# Revit family: 28798_2
name_source: partatom
category: Generic Models
units: mm (PartAtom-declared; Revit-internal decimal feet)

## family parameters
Always vertical = Yes
Can host rebar = No
Cut with Voids When Loaded = No
Part Type = Normal
Room Calculation Point = No
Round Connector Dimension = Use Diameter
Shared = Yes
Work Plane-Based = No

## types (1)
- 28798
    4.010.00.2 Sheet number of the guideline = 4
    4.010.00.4 Manufacturer name = KESSEL AG
    4.010.00.8 Producer ID number = 4026092000007
    4.100.00.4 Product indentification = Entwässerung
    4.100.00.6 Product classification = Hebeanlagen
    4.110.00.4 Product indentification = Hebeanlage Aqualift F Basic
    4.110.00.5 Main groups of wares = Aqualift F Basic
    4.110.00.6 Product classification = Hebeanlage
    4.500.00.3 Variant / Variant type / Accessories-name = Kunststoff
    4.700.00.10 Phase = 1/N/PE 230V
    4.700.00.11 Stern-/Dreieck-Anlaufschaltung bei Dreiphasenanschluss oder Drehstrom = nein
    4.700.00.12 Frequency = 50
    4.700.00.13 Type of protection = IP 68
    4.700.00.14 Heat class = F
    4.700.00.16 Maximum temperature of pumped medium = 40 °C
    4.700.00.17 Minimum temperature of pumped medium = 0 °C
    4.700.00.23 Nominal speed of motor = 10.76391
    4.700.00.24 Nominal speed / maximum speed n = 43.333333
    4.700.00.26 Maximum power consumption per pump / drive = 0
    4.700.00.27 Starting current = 6
    4.700.00.4 Product indentification = Hebeanlage Aqualift F Basic, Tronic, SPF 1300, 230 V
    4.700.00.7 Nominal connection size on pressure side = DN80, DA90
    4.700.00.8 Nominal connection size on suction side = DN80, DA90
    4.700.00.9 Voltage = 2475.699396
    4.710.01.3 Identifier for closed-loop control = 50
    4.710.01.4 Designation of closed-loop control = 20
    4.710.01.5 Load regulation = 0
    4.710.03.3 Type of dimensions = 2
    4.710.03.4 Length = 565 mm  [stored 1.85367 ft]
    4.710.03.5 Width = 624 mm  [stored 2.04724 ft]
    4.710.03.6 Height = 483 mm
    4.810.00.3 Producer order number = 28798
    4.810.00.4 DATANORM number = 28798
    4.810.00.6 GTIN number = 4026092074756
    4.810.00.7 Media- connection number = 64
    ARTICLENO = NB
    BOMINFO = LINA
    CATALOG = KESSEL
    Default Elevation = 0 mm  [stored 0 ft]
    LINA = 28798
    LINK = https://www.kessel.de
    Manufacturer = KESSEL
    Model = 28798
    NB = 28798_2
    NBSYN = $SA810ID03._$IDNR.
    NN = Lifting station Aqualift F Basic
    SA200ID03 = 6
    SA250ID03 = vertical
    SA260ID03 = dry-rotor pump
    SA350ID03 = normal-priming
    SA400ID03 = e-motor for alternating current
    SA460ID03 = direct
    SA700ID07 = 50
    SA700ID21 = 890
    SA700ID28 = durchgehend
    SA700ID29 = RWDR
    SA700ID30 = 1
    SA700ID32 = 22.00 kg
    SA700ID33 = 2 W
    SA700ID34 = 31
    SA700ID37 = 8900 mm  [stored 29.1995 ft]
    SA700ID46 = Yes
    SA700ID48 = No
    SUPPLIER = KESSEL

note: [stored X ft] marks values corroborated as IEEE doubles in the binary element streams (Revit-internal decimal feet)

## geometry (parser evidence)
native form markers: Sweep x15
no freeform markers — native parametric forms only
